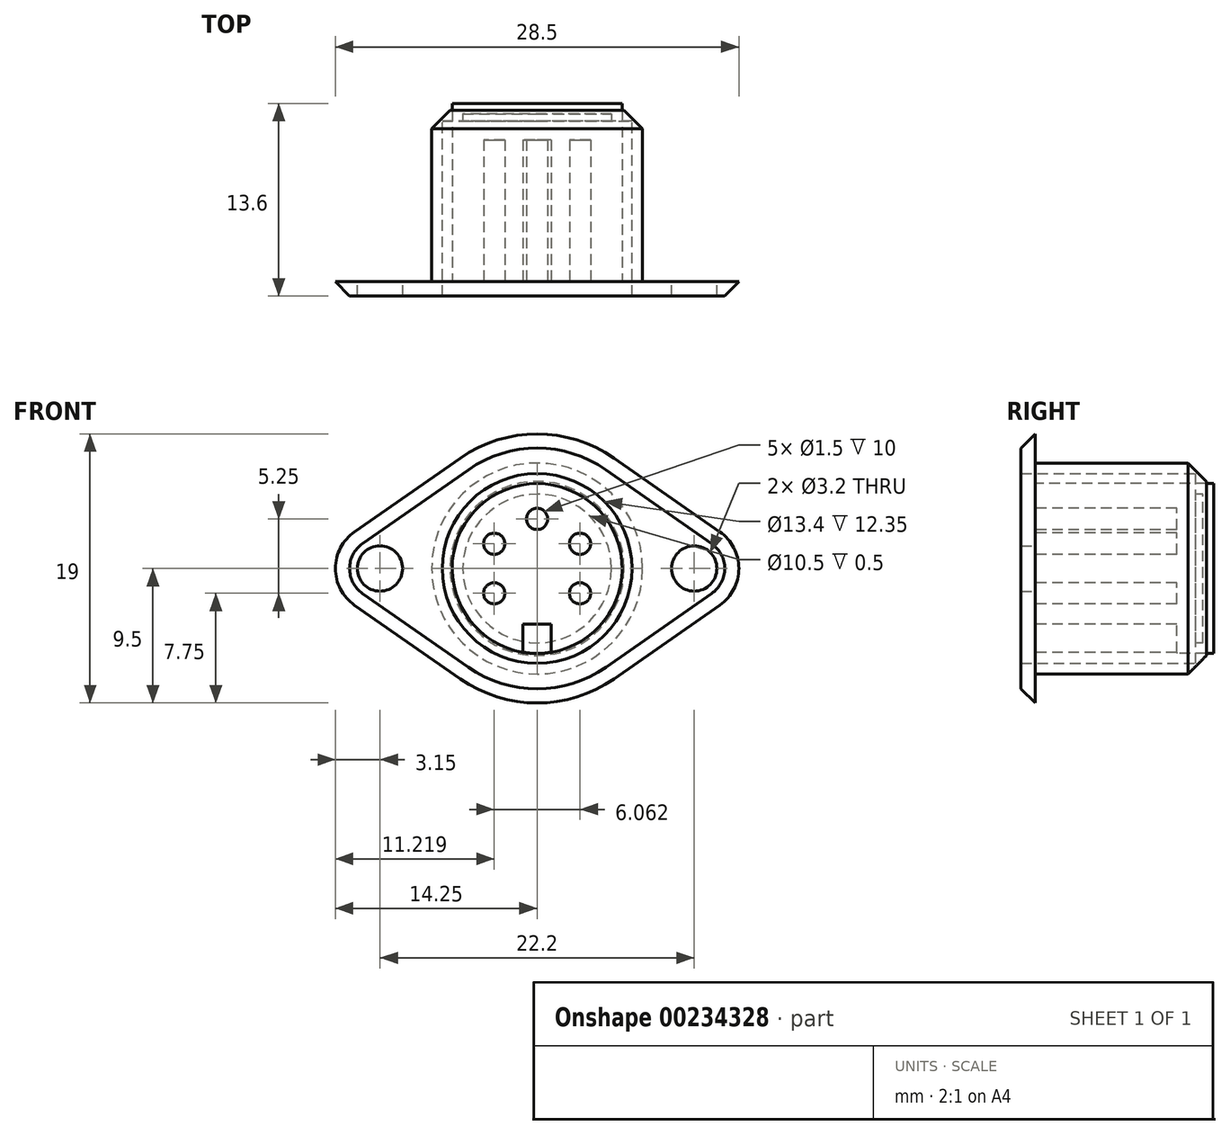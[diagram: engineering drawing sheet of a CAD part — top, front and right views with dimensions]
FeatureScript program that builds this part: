
annotation { "Feature Type Name" : "Feature", "Feature Type Description" : "" }
export const myFeature = defineFeature(function(context is Context, id is Id, definition is map)
    precondition{}
    {
        {
            var Q0;
            Q0=qCreatedBy(makeId("Front.planeOp"),FACE);
            var sketch = newSketch(context, id + "F0", { "sketchPlane" : qUnion([Q0])});
            skCircle(sketch, "E0", {"center": v(-11.1, 0) * mm, "radius": 1.6 * mm});
            skCircle(sketch, "E1", {"center": v(11.1, 0) * mm, "radius": 1.6 * mm});
            skArc(sketch, "E2", {"start": v(-12.9, 2.58) * mm, "mid": v(-14.25, 0) * mm, "end": v(-12.9, -2.58) * mm});
            skLineSegment(sketch, "E3", {"start": v(-14.25, 0) * mm, "end": v(14.25, 0) * mm, "construction": true});
            skCircle(sketch, "E4", {"center": v(0, 0) * mm, "radius": 6 * mm});
            skCircle(sketch, "E5", {"center": v(0, 0) * mm, "radius": 6.7 * mm});
            skArc(sketch, "E6", {"start": v(5.43, 7.8) * mm, "mid": v(0, 9.5) * mm, "end": v(-5.43, 7.8) * mm});
            skLineSegment(sketch, "E7", {"start": v(-12.9, 2.58) * mm, "end": v(-5.43, 7.8) * mm});
            skLineSegment(sketch, "E8", {"start": v(-12.9, -2.58) * mm, "end": v(-5.43, -7.8) * mm});
            skArc(sketch, "E9", {"start": v(12.9, -2.58) * mm, "mid": v(14.25, 0) * mm, "end": v(12.9, 2.58) * mm});
            skLineSegment(sketch, "E10", {"start": v(5.43, 7.8) * mm, "end": v(12.9, 2.58) * mm});
            skLineSegment(sketch, "E11", {"start": v(5.43, -7.8) * mm, "end": v(12.9, -2.58) * mm});
            skArc(sketch, "E12.trimOffspring", {"start": v(-5.43, -7.8) * mm, "mid": v(0, -9.5) * mm, "end": v(5.43, -7.8) * mm});
            skCircle(sketch, "E13", {"center": v(-3.03, -1.75) * mm, "radius": 0.75 * mm});
            skLineSegment(sketch, "E14", {"start": v(-1, -5.92) * mm, "end": v(-1, -3.92) * mm});
            skLineSegment(sketch, "E15", {"start": v(-1, -3.92) * mm, "end": v(0, -3.92) * mm});
            skLineSegment(sketch, "E16.MirrorCS", {"start": v(1, -3.92) * mm, "end": v(0, -3.92) * mm});
            skLineSegment(sketch, "E17.MirrorCS", {"start": v(1, -5.92) * mm, "end": v(1, -3.92) * mm});
            skCircle(sketch, "E18", {"center": v(0, 0) * mm, "radius": 7.45 * mm});
            skLineSegment(sketch, "E19", {"start": v(-1, -5.92) * mm, "end": v(-1, -6.33) * mm});
            skLineSegment(sketch, "E20", {"start": v(-1, -6.33) * mm, "end": v(1, -6.33) * mm});
            skLineSegment(sketch, "E21", {"start": v(1, -6.33) * mm, "end": v(1, -5.92) * mm});
            skLineSegment(sketch, "E22", {"start": v(0, 0) * mm, "end": v(-3.03, -1.75) * mm, "construction": true});
            skCircle(sketch, "E23.1.0", {"center": v(-3.03, 1.75) * mm, "radius": 0.75 * mm});
            skCircle(sketch, "E23.2.0", {"center": v(0, 3.5) * mm, "radius": 0.75 * mm});
            skCircle(sketch, "E23.3.0", {"center": v(3.03, 1.75) * mm, "radius": 0.75 * mm});
            skCircle(sketch, "E23.4.0", {"center": v(3.03, -1.75) * mm, "radius": 0.75 * mm});
            skLineSegment(sketch, "E23.anchor2", {"start": v(0, 0) * mm, "end": v(3.03, -1.75) * mm, "construction": true});
            skSolve(sketch);
        }
        {
            var Q0;
            Q0=makeQuery(id+"F0.imprint","IMPRINT",FACE,{"disambiguationData":[TD([[makeQuery(id+"F0.imprint","IMPRINT",EDGE,{"derivedFrom":sQuery(id+"F0.wireOp",EDGE,"E0")}),-1.0]])]});
            var Q1;
            Q1=makeQuery(id+"F0.imprint","IMPRINT",FACE,{"disambiguationData":[TD([[makeQuery(id+"F0.imprint","IMPRINT",EDGE,{"derivedFrom":sQuery(id+"F0.wireOp",EDGE,"E5")}),-1.0]])]});
            extrude(context, id + "F1", {"entities" : qUnion([Q0, Q1]), "depth" : 1 * mm});
        }
        {
            var Q0;
            Q0=makeQuery(id+"F1.opExtrude","CAP_EDGE",EDGE,{"disambiguationData":[OSD([sQuery(id+"F0.wireOp",EDGE,"E7")])],"isStart":false});
            chamfer(context, id + "F2", {"entities" : qUnion([Q0]), "width" : 1 * mm, "tangentPropagation" : true});
        }
        {
            var Q0;
            Q0=makeQuery(id+"F0.imprint","IMPRINT",FACE,{"disambiguationData":[TD([[makeQuery(id+"F0.imprint","IMPRINT",EDGE,{"derivedFrom":sQuery(id+"F0.wireOp",EDGE,"E5")}),-1.0]])]});
            var Q1;
            Q1=makeQuery(id+"F0.imprint","IMPRINT",FACE,{"disambiguationData":[TD([[makeQuery(id+"F0.imprint","IMPRINT",EDGE,{"derivedFrom":sQuery(id+"F0.wireOp",EDGE,"E5")}),1.0]])]});
            var Q2;
            Q2=makeQuery(id+"F0.imprint","IMPRINT",FACE,{"disambiguationData":[TD([[makeQuery(id+"F0.imprint","IMPRINT",EDGE,{"derivedFrom":sQuery(id+"F0.wireOp",EDGE,"E13")}),-1.0]])]});
            var Q3;
            Q3=makeQuery(id+"F0.imprint","IMPRINT",FACE,{"disambiguationData":[TD([[makeQuery(id+"F0.imprint","IMPRINT",EDGE,{"derivedFrom":sQuery(id+"F0.wireOp",EDGE,"E13")}),1.0]])]});
            var Q4;
            Q4=makeQuery(id+"F0.imprint","IMPRINT",FACE,{"disambiguationData":[TD([[makeQuery(id+"F0.imprint","IMPRINT",EDGE,{"derivedFrom":sQuery(id+"F0.wireOp",EDGE,"8ae15eba-1823-4ec1-8828-4b0b3d9a4faf.1.0")}),1.0]])]});
            var Q5;
            Q5=makeQuery(id+"F0.imprint","IMPRINT",FACE,{"disambiguationData":[TD([[makeQuery(id+"F0.imprint","IMPRINT",EDGE,{"derivedFrom":sQuery(id+"F0.wireOp",EDGE,"8ae15eba-1823-4ec1-8828-4b0b3d9a4faf.2.0")}),1.0]])]});
            var Q6;
            Q6=makeQuery(id+"F0.imprint","IMPRINT",FACE,{"disambiguationData":[TD([[makeQuery(id+"F0.imprint","IMPRINT",EDGE,{"derivedFrom":sQuery(id+"F0.wireOp",EDGE,"8ae15eba-1823-4ec1-8828-4b0b3d9a4faf.3.0")}),1.0]])]});
            var Q7;
            Q7=makeQuery(id+"F0.imprint","IMPRINT",FACE,{"disambiguationData":[TD([[makeQuery(id+"F0.imprint","IMPRINT",EDGE,{"derivedFrom":sQuery(id+"F0.wireOp",EDGE,"8ae15eba-1823-4ec1-8828-4b0b3d9a4faf.4.0")}),1.0]])]});
            var Q8;
            {var subQ0=sQuery(id+"F0.wireOp",EDGE,"E14");Q8=makeQuery(id+"F0.imprint","IMPRINT",FACE,{"disambiguationData":[TD([[makeQuery(id+"F0.imprint","IMPRINT",EDGE,{"derivedFrom":subQ0}),-1.0]])]});}
            var Q9;
            {var subQ0=sQuery(id+"F0.wireOp",EDGE,"E19");Q9=makeQuery(id+"F0.imprint","IMPRINT",FACE,{"disambiguationData":[TD([[makeQuery(id+"F0.imprint","IMPRINT",EDGE,{"derivedFrom":subQ0}),1.0]])]});}
            var Q10;
            Q10=makeQuery(id+"F0.imprint","IMPRINT",FACE,{"disambiguationData":[TD([[makeQuery(id+"F0.imprint","IMPRINT",EDGE,{"derivedFrom":sQuery(id+"F0.wireOp",EDGE,"E23.1.0")}),1.0]])]});
            var Q11;
            Q11=makeQuery(id+"F0.imprint","IMPRINT",FACE,{"disambiguationData":[TD([[makeQuery(id+"F0.imprint","IMPRINT",EDGE,{"derivedFrom":sQuery(id+"F0.wireOp",EDGE,"E23.2.0")}),1.0]])]});
            var Q12;
            Q12=makeQuery(id+"F0.imprint","IMPRINT",FACE,{"disambiguationData":[TD([[makeQuery(id+"F0.imprint","IMPRINT",EDGE,{"derivedFrom":sQuery(id+"F0.wireOp",EDGE,"E23.3.0")}),1.0]])]});
            var Q13;
            Q13=makeQuery(id+"F0.imprint","IMPRINT",FACE,{"disambiguationData":[TD([[makeQuery(id+"F0.imprint","IMPRINT",EDGE,{"derivedFrom":sQuery(id+"F0.wireOp",EDGE,"E23.4.0")}),1.0]])]});
            var Q14;
            Q14=sQuery(id+"F0.wireOp",EDGE,"E5");
            extrude(context, id + "F3", {"entities" : qUnion([Q0, Q1, Q2, Q3, Q4, Q5, Q6, Q7, Q8, Q9, Q10, Q11, Q12, Q13]), "operationType" : NewBodyOperationType.ADD, "surfaceEntities" : qUnion([Q14]), "oppositeDirection" : true, "depth" : 12.1 * mm, "offsetDistance" : 25 * mm});
        }
        {
            var Q0;
            Q0=makeQuery(id+"F3.opExtrude","CAP_FACE",FACE,{"disambiguationData":[OSD([sQuery(id+"F0.wireOp",EDGE,"E18")])],"isStart":true});
            shell(context, id + "F4", {"entities" : qUnion([Q0]), "thickness" : .75 * mm});
        }
        {
            var Q0;
            Q0=makeQuery(id+"F0.imprint","IMPRINT",FACE,{"disambiguationData":[TD([[makeQuery(id+"F0.imprint","IMPRINT",EDGE,{"derivedFrom":sQuery(id+"F0.wireOp",EDGE,"E13")}),-1.0]])]});
            var Q1;
            Q1=makeQuery(id+"F0.imprint","IMPRINT",FACE,{"disambiguationData":[TD([[makeQuery(id+"F0.imprint","IMPRINT",EDGE,{"derivedFrom":sQuery(id+"F0.wireOp",EDGE,"E13")}),1.0]])]});
            var Q2;
            Q2=makeQuery(id+"F0.imprint","IMPRINT",FACE,{"disambiguationData":[TD([[makeQuery(id+"F0.imprint","IMPRINT",EDGE,{"derivedFrom":sQuery(id+"F0.wireOp",EDGE,"8ae15eba-1823-4ec1-8828-4b0b3d9a4faf.1.0")}),1.0]])]});
            var Q3;
            Q3=makeQuery(id+"F0.imprint","IMPRINT",FACE,{"disambiguationData":[TD([[makeQuery(id+"F0.imprint","IMPRINT",EDGE,{"derivedFrom":sQuery(id+"F0.wireOp",EDGE,"8ae15eba-1823-4ec1-8828-4b0b3d9a4faf.2.0")}),1.0]])]});
            var Q4;
            Q4=makeQuery(id+"F0.imprint","IMPRINT",FACE,{"disambiguationData":[TD([[makeQuery(id+"F0.imprint","IMPRINT",EDGE,{"derivedFrom":sQuery(id+"F0.wireOp",EDGE,"8ae15eba-1823-4ec1-8828-4b0b3d9a4faf.3.0")}),1.0]])]});
            var Q5;
            Q5=makeQuery(id+"F0.imprint","IMPRINT",FACE,{"disambiguationData":[TD([[makeQuery(id+"F0.imprint","IMPRINT",EDGE,{"derivedFrom":sQuery(id+"F0.wireOp",EDGE,"8ae15eba-1823-4ec1-8828-4b0b3d9a4faf.4.0")}),1.0]])]});
            var Q6;
            {var subQ0=sQuery(id+"F0.wireOp",EDGE,"E14");Q6=makeQuery(id+"F0.imprint","IMPRINT",FACE,{"disambiguationData":[TD([[makeQuery(id+"F0.imprint","IMPRINT",EDGE,{"derivedFrom":subQ0}),-1.0]])]});}
            var Q7;
            Q7=makeQuery(id+"F0.imprint","IMPRINT",FACE,{"disambiguationData":[TD([[makeQuery(id+"F0.imprint","IMPRINT",EDGE,{"derivedFrom":sQuery(id+"F0.wireOp",EDGE,"E23.1.0")}),1.0]])]});
            var Q8;
            Q8=makeQuery(id+"F0.imprint","IMPRINT",FACE,{"disambiguationData":[TD([[makeQuery(id+"F0.imprint","IMPRINT",EDGE,{"derivedFrom":sQuery(id+"F0.wireOp",EDGE,"E23.2.0")}),1.0]])]});
            var Q9;
            Q9=makeQuery(id+"F0.imprint","IMPRINT",FACE,{"disambiguationData":[TD([[makeQuery(id+"F0.imprint","IMPRINT",EDGE,{"derivedFrom":sQuery(id+"F0.wireOp",EDGE,"E23.3.0")}),1.0]])]});
            var Q10;
            Q10=makeQuery(id+"F0.imprint","IMPRINT",FACE,{"disambiguationData":[TD([[makeQuery(id+"F0.imprint","IMPRINT",EDGE,{"derivedFrom":sQuery(id+"F0.wireOp",EDGE,"E23.4.0")}),1.0]])]});
            extrude(context, id + "F5", {"entities" : qUnion([Q0, Q1, Q2, Q3, Q4, Q5, Q6, Q7, Q8, Q9, Q10]), "oppositeDirection" : true, "depth" : 12.6 * mm, "offsetDistance" : 25 * mm});
        }
        {
            var Q0;
            Q0=makeQuery(id+"F0.imprint","IMPRINT",FACE,{"disambiguationData":[TD([[makeQuery(id+"F0.imprint","IMPRINT",EDGE,{"derivedFrom":sQuery(id+"F0.wireOp",EDGE,"E13")}),1.0]])]});
            var Q1;
            {var subQ0=sQuery(id+"F0.wireOp",EDGE,"E14");Q1=makeQuery(id+"F0.imprint","IMPRINT",FACE,{"disambiguationData":[TD([[makeQuery(id+"F0.imprint","IMPRINT",EDGE,{"derivedFrom":subQ0}),-1.0]])]});}
            var Q2;
            Q2=makeQuery(id+"F0.imprint","IMPRINT",FACE,{"disambiguationData":[TD([[makeQuery(id+"F0.imprint","IMPRINT",EDGE,{"derivedFrom":sQuery(id+"F0.wireOp",EDGE,"8ae15eba-1823-4ec1-8828-4b0b3d9a4faf.1.0")}),1.0]])]});
            var Q3;
            Q3=makeQuery(id+"F0.imprint","IMPRINT",FACE,{"disambiguationData":[TD([[makeQuery(id+"F0.imprint","IMPRINT",EDGE,{"derivedFrom":sQuery(id+"F0.wireOp",EDGE,"8ae15eba-1823-4ec1-8828-4b0b3d9a4faf.2.0")}),1.0]])]});
            var Q4;
            Q4=makeQuery(id+"F0.imprint","IMPRINT",FACE,{"disambiguationData":[TD([[makeQuery(id+"F0.imprint","IMPRINT",EDGE,{"derivedFrom":sQuery(id+"F0.wireOp",EDGE,"8ae15eba-1823-4ec1-8828-4b0b3d9a4faf.3.0")}),1.0]])]});
            var Q5;
            Q5=makeQuery(id+"F0.imprint","IMPRINT",FACE,{"disambiguationData":[TD([[makeQuery(id+"F0.imprint","IMPRINT",EDGE,{"derivedFrom":sQuery(id+"F0.wireOp",EDGE,"8ae15eba-1823-4ec1-8828-4b0b3d9a4faf.4.0")}),1.0]])]});
            var Q6;
            Q6=makeQuery(id+"F0.imprint","IMPRINT",FACE,{"disambiguationData":[TD([[makeQuery(id+"F0.imprint","IMPRINT",EDGE,{"derivedFrom":sQuery(id+"F0.wireOp",EDGE,"E23.1.0")}),1.0]])]});
            var Q7;
            Q7=makeQuery(id+"F0.imprint","IMPRINT",FACE,{"disambiguationData":[TD([[makeQuery(id+"F0.imprint","IMPRINT",EDGE,{"derivedFrom":sQuery(id+"F0.wireOp",EDGE,"E23.2.0")}),1.0]])]});
            var Q8;
            Q8=makeQuery(id+"F0.imprint","IMPRINT",FACE,{"disambiguationData":[TD([[makeQuery(id+"F0.imprint","IMPRINT",EDGE,{"derivedFrom":sQuery(id+"F0.wireOp",EDGE,"E23.3.0")}),1.0]])]});
            var Q9;
            Q9=makeQuery(id+"F0.imprint","IMPRINT",FACE,{"disambiguationData":[TD([[makeQuery(id+"F0.imprint","IMPRINT",EDGE,{"derivedFrom":sQuery(id+"F0.wireOp",EDGE,"E23.4.0")}),1.0]])]});
            extrude(context, id + "F6", {"entities" : qUnion([Q0, Q1, Q2, Q3, Q4, Q5, Q6, Q7, Q8, Q9]), "operationType" : NewBodyOperationType.REMOVE, "oppositeDirection" : true, "depth" : 10 * mm, "offsetDistance" : 25 * mm});
        }
        {
            var Q0;
            Q0=makeQuery(id+"F3.opExtrude","CAP_EDGE",EDGE,{"disambiguationData":[OSD([sQuery(id+"F0.wireOp",EDGE,"E18")])],"isStart":false});
            chamfer(context, id + "F7", {"entities" : qUnion([Q0]), "width" : 1.3 * mm, "tangentPropagation" : true});
        }
    });
